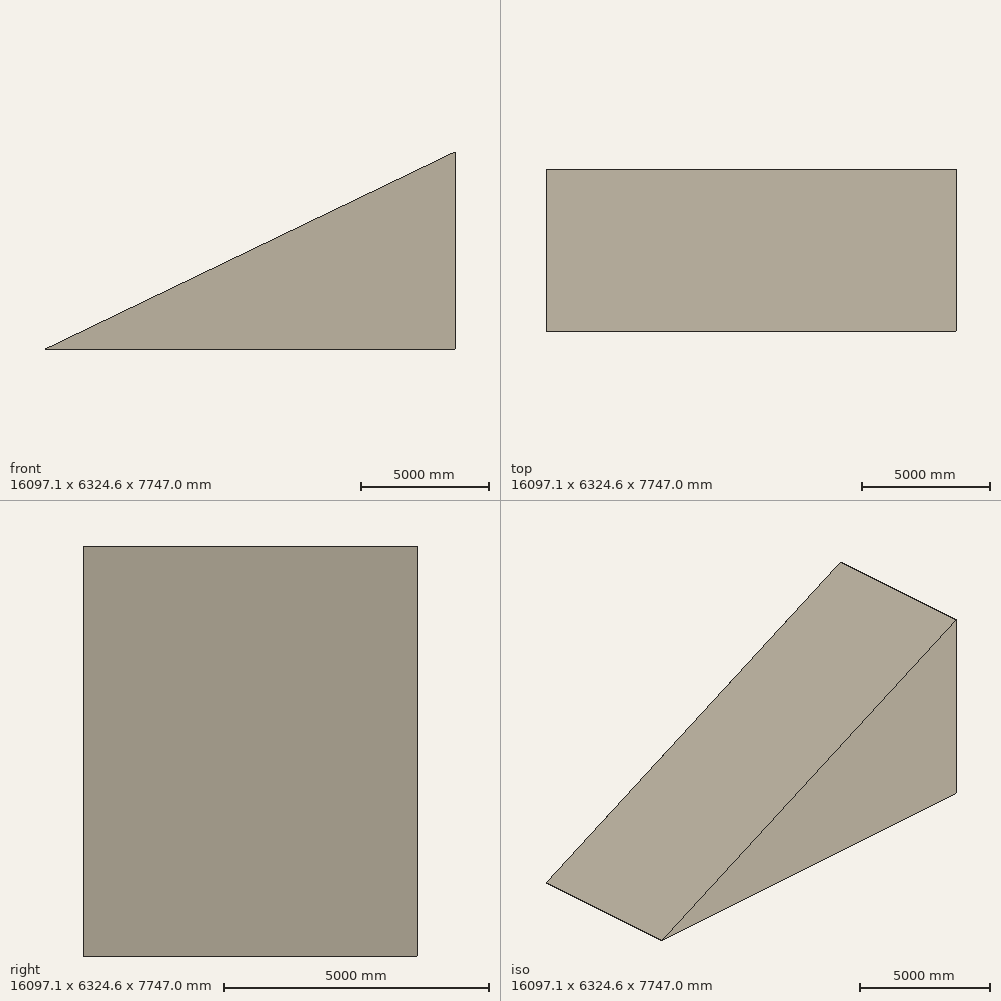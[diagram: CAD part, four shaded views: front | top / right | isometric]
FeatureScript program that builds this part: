
annotation { "Feature Type Name" : "Feature", "Feature Type Description" : "" }
export const myFeature = defineFeature(function(context is Context, id is Id, definition is map)
    precondition{}
    {
        {
            var Q0;
            Q0=qCreatedBy(makeId("Front.planeOp"),FACE);
            var sketch = newSketch(context, id + "F0", { "sketchPlane" : qUnion([Q0])});
            skLineSegment(sketch, "E0", {"start": v(-7512.2, -3845.43) * mm, "end": v(8584.88, -3845.43) * mm});
            skLineSegment(sketch, "E1", {"start": v(8584.88, -3845.43) * mm, "end": v(8584.88, 3901.57) * mm});
            skLineSegment(sketch, "E2", {"start": v(8584.88, 3901.57) * mm, "end": v(-7512.2, -3845.43) * mm});
            skSolve(sketch);
        }
        {
            var Q0;
            Q0=makeQuery(id+"F0.imprint","IMPRINT",FACE,{"disambiguationData":[TD([[makeQuery(id+"F0.imprint","IMPRINT",EDGE,{"derivedFrom":sQuery(id+"F0.wireOp",EDGE,"E0")}),1.0]])]});
            extrude(context, id + "F1", {"entities" : qUnion([Q0]), "depth" : 6324.6 * mm});
        }
    });
